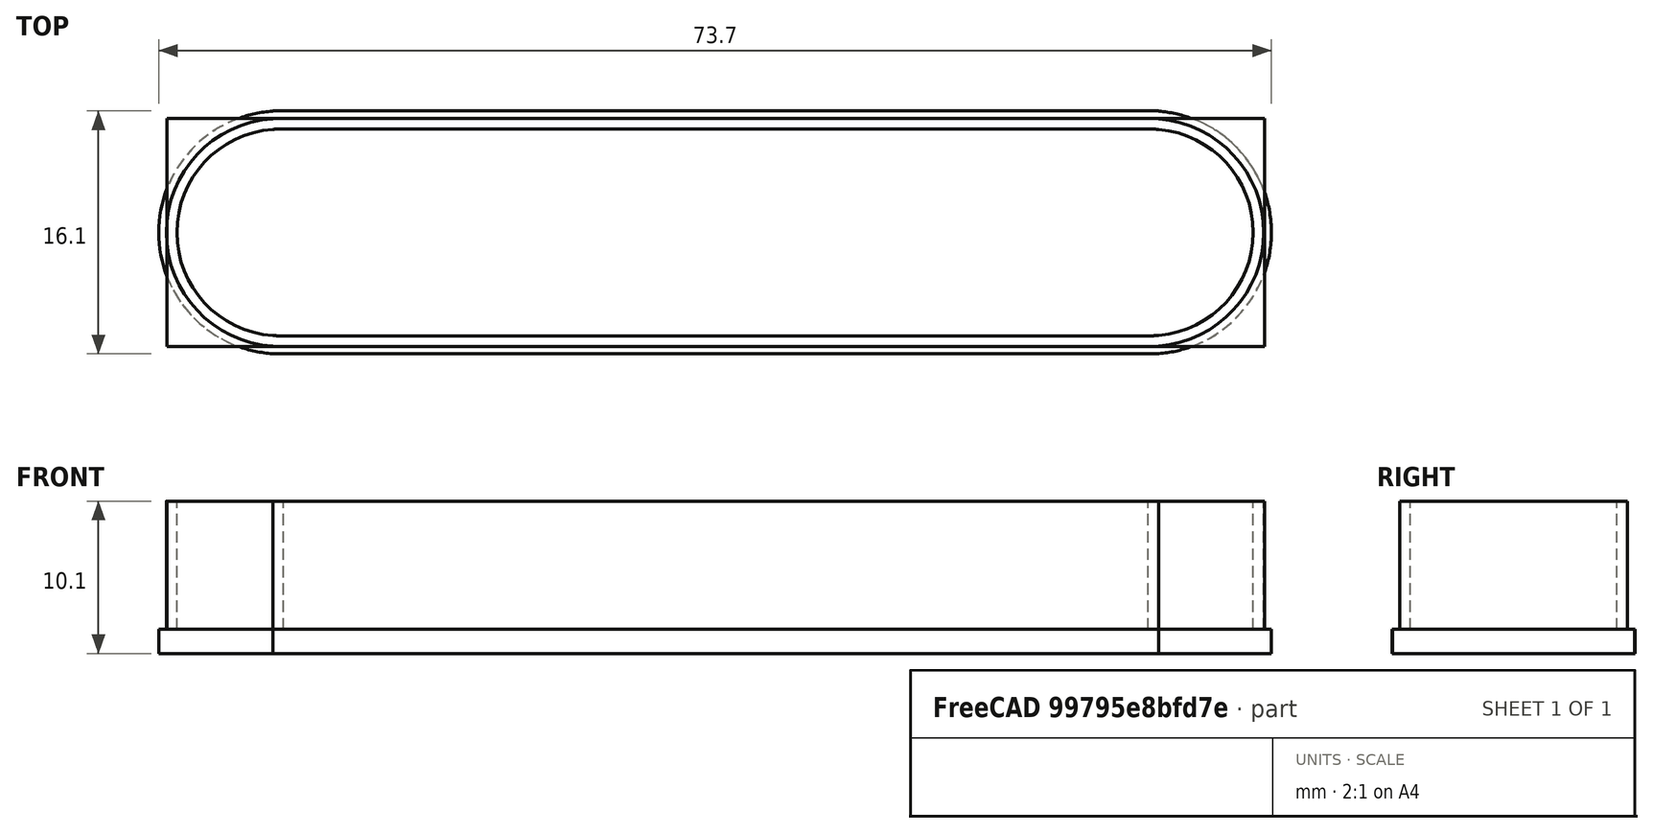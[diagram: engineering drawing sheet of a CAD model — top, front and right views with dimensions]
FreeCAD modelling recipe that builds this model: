
FCSTD DOCUMENT  (FreeCAD 0.18.4R)
Label: tappo-bauletto-givi
License: All rights reserved
LicenseURL: http://en.wikipedia.org/wiki/All_rights_reserved
objects: Part::Cylinder×6, Part::Box×4, Part::MultiFuse×4, Part::Cut×1
note: 15 computed .brp shape members not serialized (recipe doc carries the construction recipe); baked Part::Feature solids carry a one-line shape summary decoded from their .brp

FEATURE [Part::Box] Box  label="Cube"
  AttacherType = Attacher::AttachEngine3D
  Height = 8.5
  Length = 72.7
  Width = 15.1
FEATURE [Part::Cylinder] Cylinder
  Angle = 360
  AttacherType = Attacher::AttachEngine3D
  Height = 8.5
  Placement = pos=(7.5,7.55,0) rot=(0,0,1;0rad)
  Radius = 7.55
FEATURE [Part::Cylinder] Cylinder001
  Angle = 360
  AttacherType = Attacher::AttachEngine3D
  Height = 8.5
  Placement = pos=(65.1,7.55,0) rot=(0,0,1;0rad)
  Radius = 7.55
FEATURE [Part::Box] Box001  label="Cube001"
  AttacherType = Attacher::AttachEngine3D
  Height = 8.5
  Length = 58.7
  Placement = pos=(7,0,0) rot=(0,0,1;0rad)
  Width = 15.1
FEATURE [Part::Cylinder] Cylinder002
  Angle = 360
  AttacherType = Attacher::AttachEngine3D
  Height = 1.6
  Placement = pos=(7.5,7.55,0) rot=(0,0,1;0rad)
  Radius = 8.05
FEATURE [Part::Cylinder] Cylinder003
  Angle = 360
  AttacherType = Attacher::AttachEngine3D
  Height = 1.6
  Placement = pos=(65.1,7.55,0) rot=(0,0,1;0rad)
  Radius = 8.05
FEATURE [Part::Box] Box002  label="Cube002"
  AttacherType = Attacher::AttachEngine3D
  Height = 1.6
  Length = 58.7
  Placement = pos=(7,-0.5,0) rot=(0,0,1;0rad)
  Width = 16.1
FEATURE [Part::Box] Box003  label="Cube003"
  AttacherType = Attacher::AttachEngine3D
  Height = 8.5
  Length = 57.3
  Placement = pos=(7.7,0.7,0) rot=(0,0,1;0rad)
  Width = 13.7
FEATURE [Part::Cylinder] Cylinder004
  Angle = 360
  AttacherType = Attacher::AttachEngine3D
  Height = 8.5
  Placement = pos=(65.1,7.55,0) rot=(0,0,1;0rad)
  Radius = 6.85
FEATURE [Part::Cylinder] Cylinder005
  Angle = 360
  AttacherType = Attacher::AttachEngine3D
  Height = 8.5
  Placement = pos=(7.5,7.55,0) rot=(0,0,1;0rad)
  Radius = 6.85
FEATURE [Part::MultiFuse] Fusion
  Shapes = -> [Cylinder,Cylinder001,Box001]
FEATURE [Part::MultiFuse] Fusion001
  Shapes = -> [Box003,Cylinder004,Cylinder005]
FEATURE [Part::Cut] Cut
  Base = -> Fusion
  Tool = -> Fusion001
FEATURE [Part::MultiFuse] Fusion002
  Placement = pos=(0,0,-1.6) rot=(0,0,1;0rad)
  Shapes = -> [Cylinder002,Cylinder003,Box002]
FEATURE [Part::MultiFuse] Fusion003
  Shapes = -> [Cut,Fusion002]
